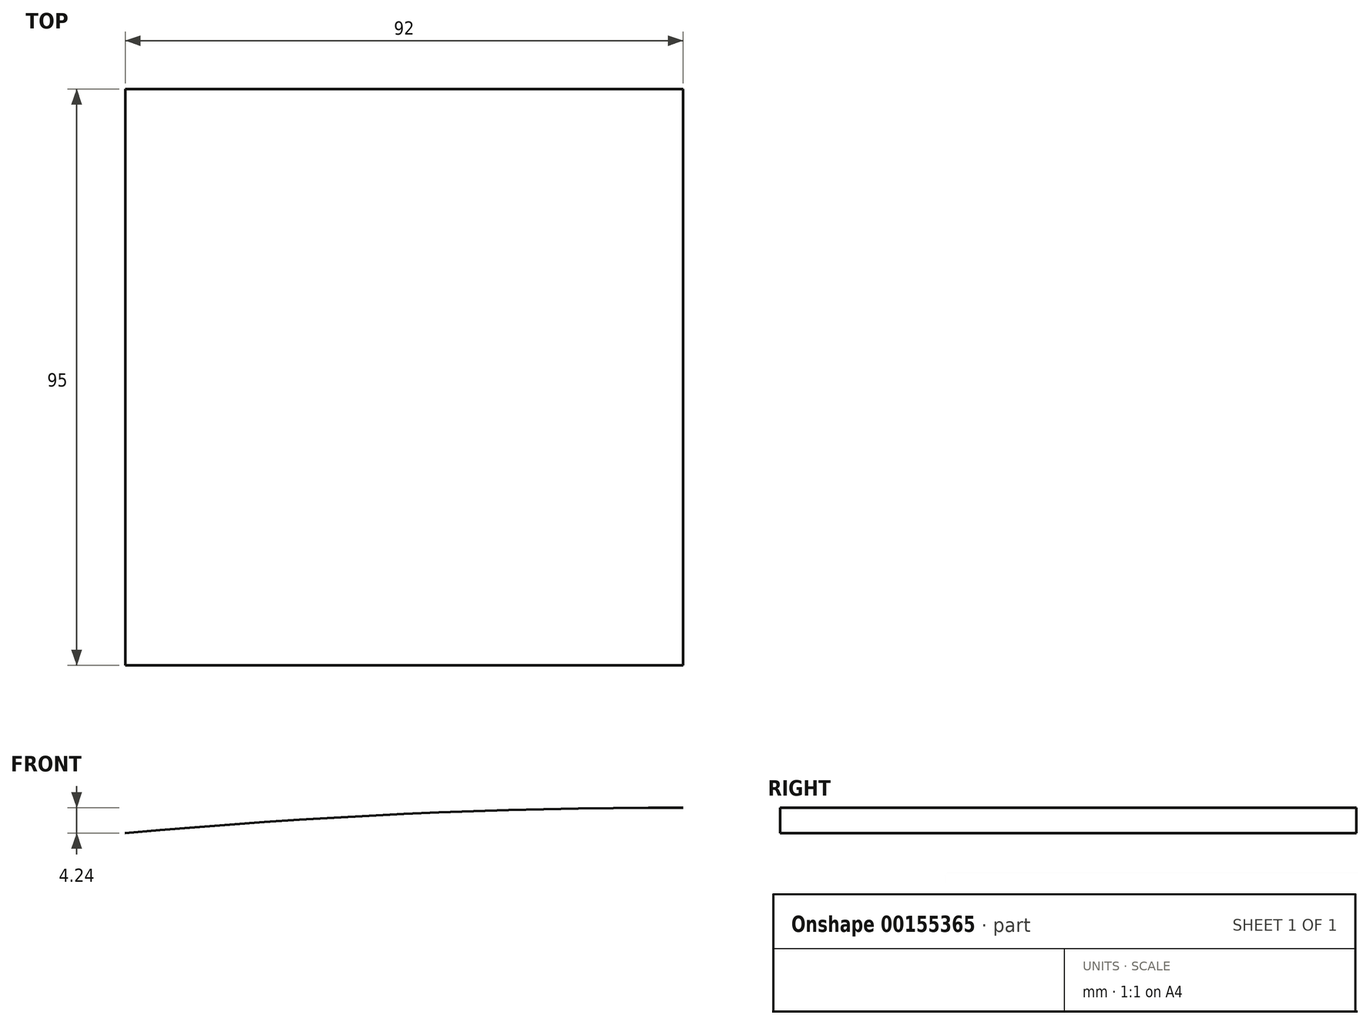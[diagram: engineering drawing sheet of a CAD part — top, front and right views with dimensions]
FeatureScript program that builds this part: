
annotation { "Feature Type Name" : "Feature", "Feature Type Description" : "" }
export const myFeature = defineFeature(function(context is Context, id is Id, definition is map)
    precondition{}
    {
        {
            var Q0;
            Q0=qCreatedBy(makeId("Front.planeOp"),FACE);
            var sketch = newSketch(context, id + "F0", { "sketchPlane" : qUnion([Q0])});
            skArc(sketch, "E0", {"start": v(-92, 65.76) * mm, "mid": v(-46.05, 68.94) * mm, "end": v(0, 70) * mm});
            skSolve(sketch);
        }
        {
            var Q0;
            Q0 = qConstructionFilter(qBodyType(qCreatedBy(id + "F0" ,EDGE), BodyType.WIRE), ConstructionObject.NO);
            extrude(context, id + "F1", {"bodyType" : ToolBodyType.SURFACE, "surfaceEntities" : qUnion([Q0]), "endBound" : BoundingType.SYMMETRIC, "depth" : (75 + 2 * 10) * mm, "hasSecondDirection" : true, "secondDirectionOppositeDirection" : true, "secondDirectionDepth" : 100 * mm});
        }
        {
            var Q0;
            Q0=qCreatedBy(makeId("Top.planeOp"),FACE);
            cPlane(context, id + "F2", {"entities" : qUnion([Q0]), "cplaneType" : CPlaneType.OFFSET, "offset" : 2.5 * mm, "oppositeDirection" : true, "width" : 150 * mm, "height" : 150 * mm});
        }
        {
            var Q0;
            Q0=qCreatedBy(id+"F2.planeOp",FACE);
            cPlane(context, id + "F3", {"entities" : qUnion([Q0]), "cplaneType" : CPlaneType.OFFSET, "offset" : 2.5 * mm, "oppositeDirection" : true, "width" : 150 * mm, "height" : 150 * mm});
        }
        {
            var Q0;
            Q0=qCreatedBy(makeId("Top.planeOp"),FACE);
            cPlane(context, id + "F4", {"entities" : qUnion([Q0]), "cplaneType" : CPlaneType.OFFSET, "offset" : 75 * mm, "width" : 150 * mm, "height" : 150 * mm});
        }
    });
